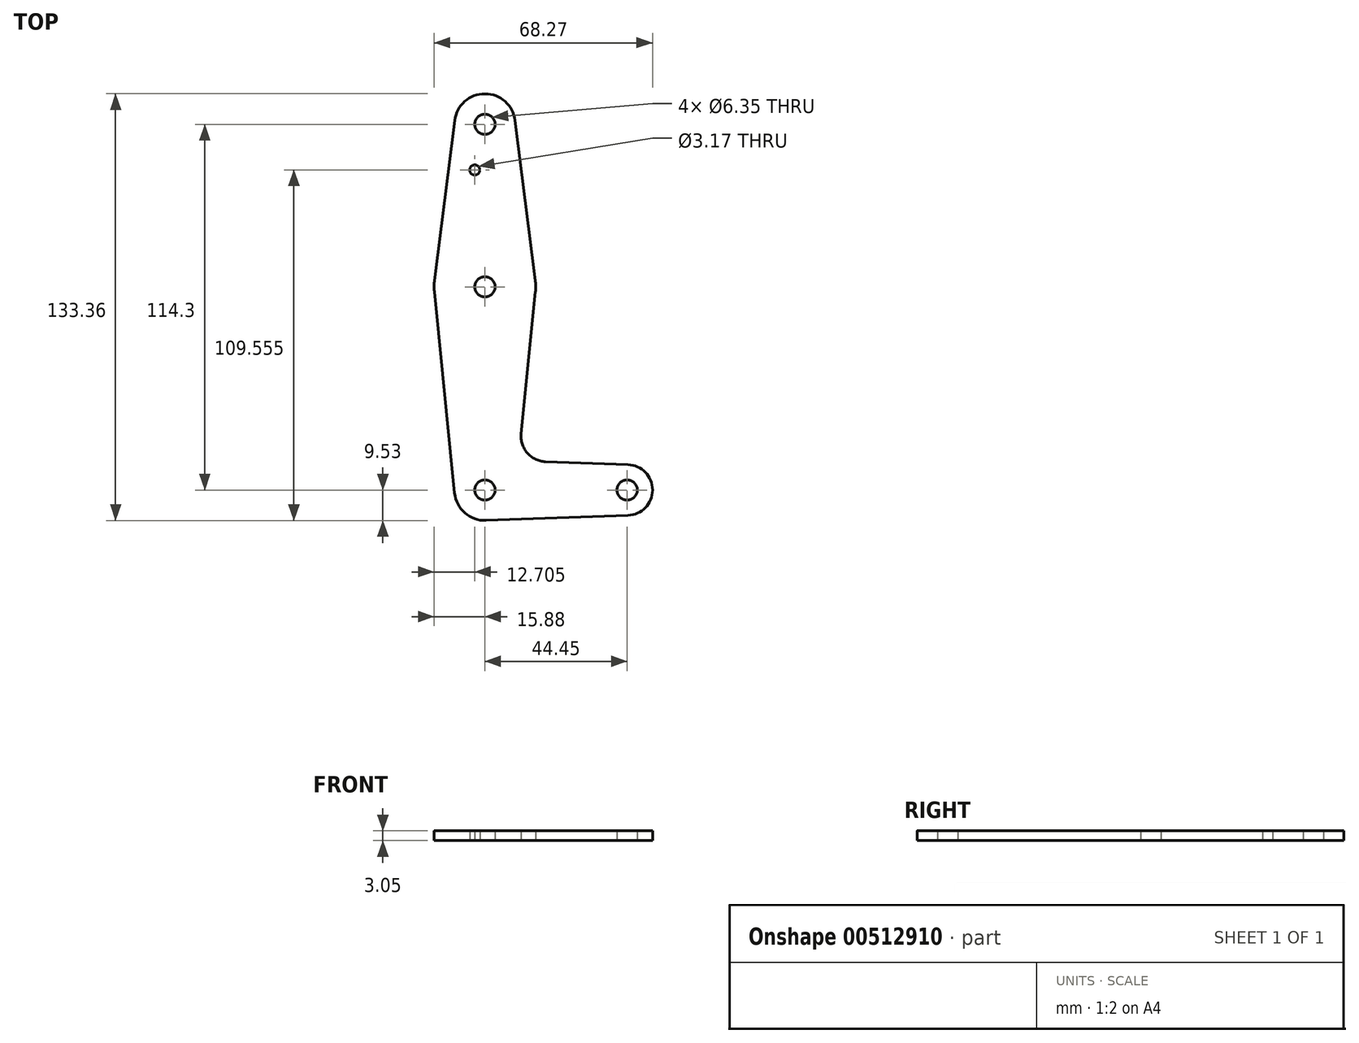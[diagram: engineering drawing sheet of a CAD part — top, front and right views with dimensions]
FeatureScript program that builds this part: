
annotation { "Feature Type Name" : "Feature", "Feature Type Description" : "" }
export const myFeature = defineFeature(function(context is Context, id is Id, definition is map)
    precondition{}
    {
        {
            var Q0;
            Q0=qCreatedBy(makeId("Top.planeOp"),FACE);
            var sketch = newSketch(context, id + "F0", { "sketchPlane" : qUnion([Q0])});
            skArc(sketch, "E0", {"start": v(-9.48, -0.95) * mm, "mid": v(-6.26, -7.18) * mm, "end": v(0.34, -9.52) * mm});
            skArc(sketch, "E1", {"start": v(44.73, -7.93) * mm, "mid": v(52.39, 0) * mm, "end": v(44.73, 7.93) * mm});
            skArc(sketch, "E2", {"start": v(15.8, 61.91) * mm, "mid": v(15.87, 63.7) * mm, "end": v(15.75, 65.48) * mm});
            skArc(sketch, "E3", {"start": v(9.45, 115.5) * mm, "mid": v(0, 123.83) * mm, "end": v(-9.45, 115.5) * mm});
            skLineSegment(sketch, "E4", {"start": v(9.45, 115.5) * mm, "end": v(15.75, 65.48) * mm});
            skLineSegment(sketch, "E5", {"start": v(-9.45, 115.5) * mm, "end": v(-15.75, 65.48) * mm});
            skLineSegment(sketch, "E6", {"start": v(15.8, 61.91) * mm, "end": v(11.34, 17.6) * mm});
            skLineSegment(sketch, "E7", {"start": v(-15.8, 61.91) * mm, "end": v(-9.48, -0.95) * mm});
            skLineSegment(sketch, "E8", {"start": v(44.73, -7.93) * mm, "end": v(0.34, -9.52) * mm});
            skLineSegment(sketch, "E9", {"start": v(44.73, 7.93) * mm, "end": v(18.97, 8.85) * mm});
            skCircle(sketch, "E10", {"center": v(44.45, 0) * mm, "radius": 3.18 * mm});
            skCircle(sketch, "E11", {"center": v(0, 0) * mm, "radius": 3.18 * mm});
            skCircle(sketch, "E12", {"center": v(0, 63.5) * mm, "radius": 3.18 * mm});
            skCircle(sketch, "E13", {"center": v(0, 114.3) * mm, "radius": 3.18 * mm});
            skCircle(sketch, "E14", {"center": v(-3.18, 100.03) * mm, "radius": 1.59 * mm});
            skArc(sketch, "E15.filletArc", {"start": v(11.34, 17.6) * mm, "mid": v(13.26, 11.57) * mm, "end": v(18.97, 8.85) * mm});
            skArc(sketch, "E16.trimOffspring", {"start": v(-15.75, 65.48) * mm, "mid": v(-15.87, 63.7) * mm, "end": v(-15.8, 61.91) * mm});
            skSolve(sketch);
        }
        {
            var Q0;
            Q0 = qSketchRegion(id + "F0", true);
            extrude(context, id + "F1", {"entities" : qUnion([Q0]), "depth" : 3.05 * mm});
        }
    });
